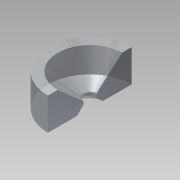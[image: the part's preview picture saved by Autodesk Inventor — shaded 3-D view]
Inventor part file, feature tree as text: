
AUTODESK INVENTOR PART (.ipt)
format: ipt  version: 2014 (Build 180170000, 170)  size: 125,440 bytes
history: native  units: mm
features: other x3, revolve x1, fillet x1, sketch x1
ambient origin geometry x8: Origin, YZ Plane, XZ Plane, XY Plane, X Axis, Y Axis, Z Axis, Center Point
bodies: Body1 (feature_tree)
feature tree (6):
  other  "CrossSection1"
  other  "CrossSection2"
  other  "CrossSection3"
  revolve  "Revolution2"  [1 undecoded]
  fillet  "Fillet4"  Radius=6.5mm
  sketch  "Sketch2"  dims[d4=5.0mm d5=1.5mm d11=6.5mm d13=90.0deg d19=0.5mm d20=2.0mm d21=0.0mm d22=20.0mm d26=4.5mm d27=0.5mm d28=1.0mm d29=2.0mm d30=0.2mm d31=1.0mm d32=0.5mm d33=2.0mm d34=0.0mm d35=20.0mm d36=0.5mm d37=2.0mm d38=0.0mm d39=20.0mm]
note: 1 required parameter value undecoded (feature->parameter linkage not recoverable at this tier; creation-order binding heuristic only, values carry confidence <= 0.55)
